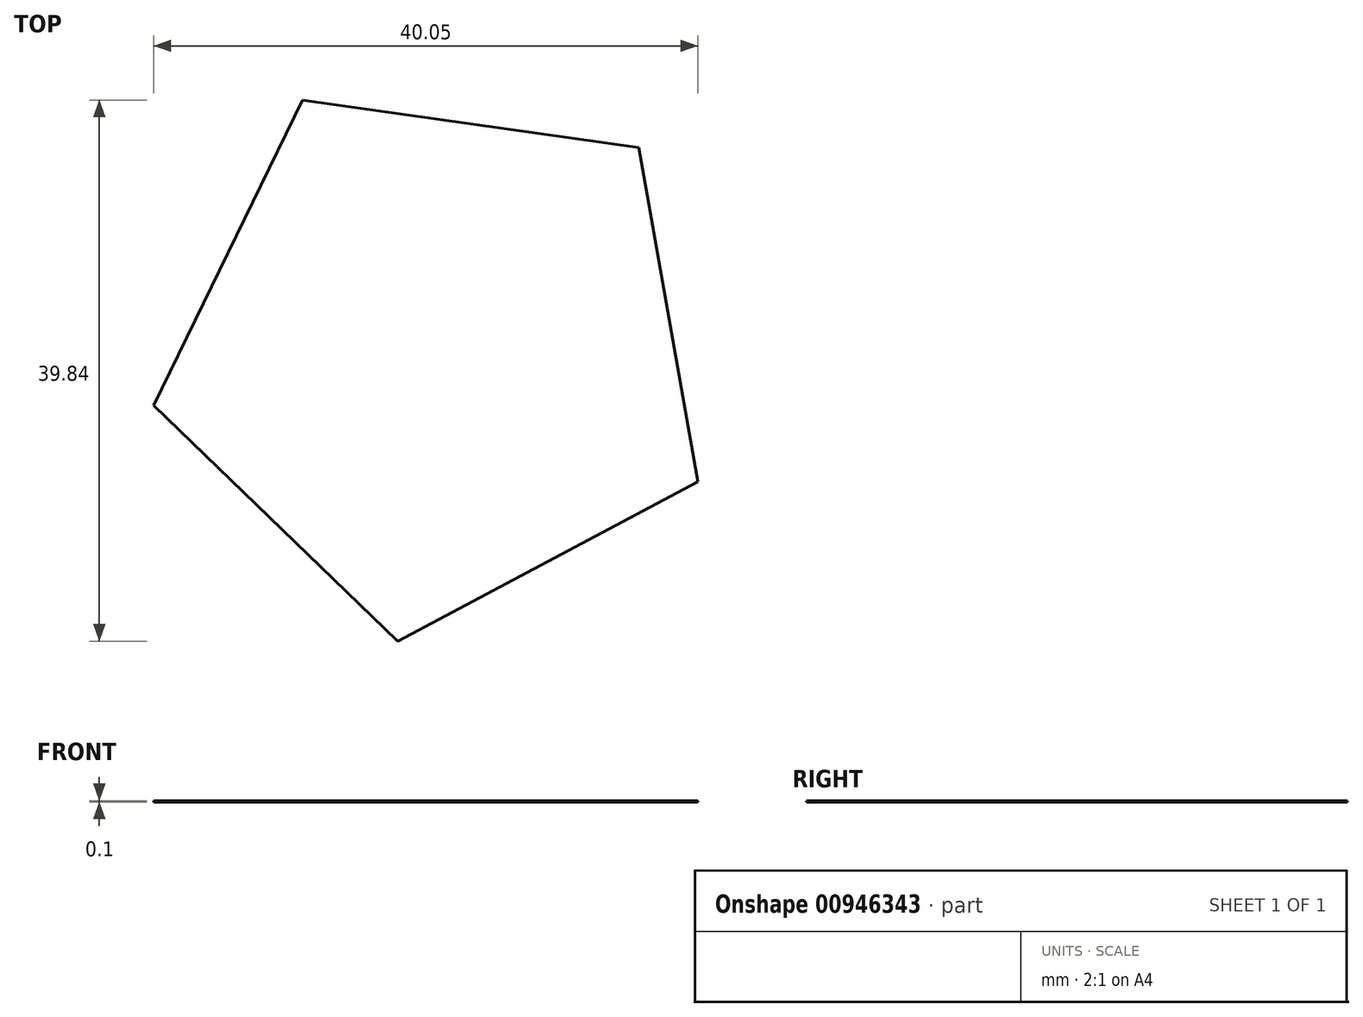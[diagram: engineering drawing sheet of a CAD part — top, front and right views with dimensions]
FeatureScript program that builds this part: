
annotation { "Feature Type Name" : "Feature", "Feature Type Description" : "" }
export const myFeature = defineFeature(function(context is Context, id is Id, definition is map)
    precondition{}
    {
        {
            var Q0;
            Q0=qCreatedBy(makeId("Top.planeOp"),FACE);
            var sketch = newSketch(context, id + "F0", { "sketchPlane" : qUnion([Q0])});
            skCircle(sketch, "E0.cCircle", {"center": v(0, 0) * mm, "radius": 17.2 * mm, "construction": true});
            skLineSegment(sketch, "E0.0", {"start": v(19.11, -9.33) * mm, "end": v(-2.97, -21.06) * mm});
            skLineSegment(sketch, "E0.1", {"start": v(-2.97, -21.06) * mm, "end": v(-20.94, -3.69) * mm});
            skLineSegment(sketch, "E0.2", {"start": v(-20.94, -3.69) * mm, "end": v(-9.98, 18.78) * mm});
            skLineSegment(sketch, "E0.3", {"start": v(-9.98, 18.78) * mm, "end": v(14.78, 15.3) * mm});
            skLineSegment(sketch, "E0.4", {"start": v(14.78, 15.3) * mm, "end": v(19.11, -9.33) * mm});
            skPoint(sketch, "E0.0.midPoint", {"position": v(8.07, -15.2) * mm});
            skSolve(sketch);
        }
        {
            var Q0;
            Q0=makeQuery(id+"F0.imprint","IMPRINT",FACE,{"disambiguationData":[TD([[makeQuery(id+"F0.imprint","IMPRINT",EDGE,{"derivedFrom":sQuery(id+"F0.wireOp",EDGE,"E0.0")}),-1.0]])]});
            extrude(context, id + "F1", {"entities" : qUnion([Q0]), "depth" : 0.1 * mm, "offsetDistance" : 25 * mm});
        }
    });
